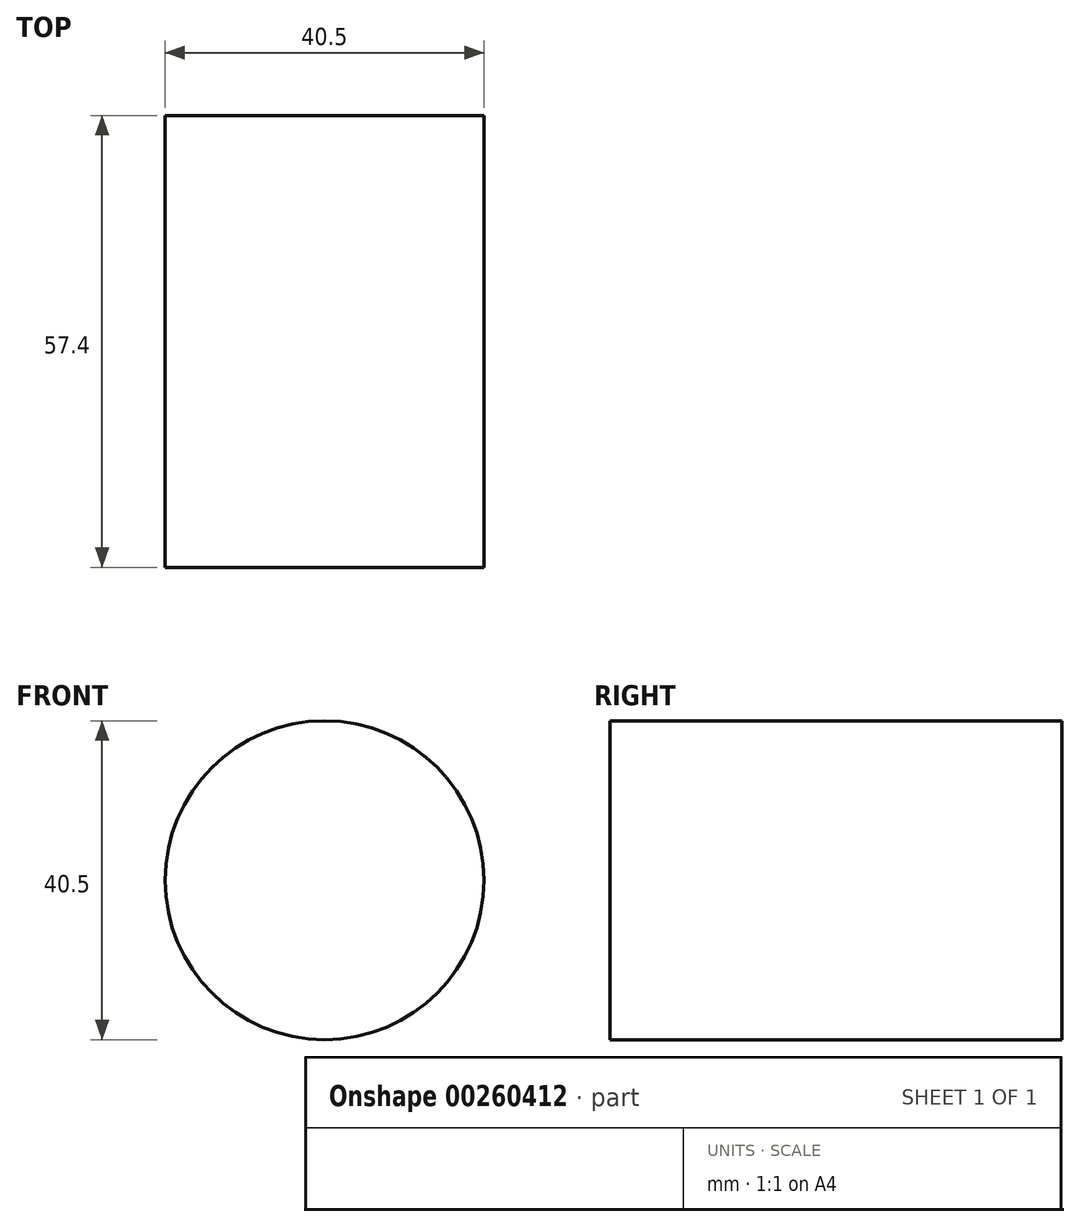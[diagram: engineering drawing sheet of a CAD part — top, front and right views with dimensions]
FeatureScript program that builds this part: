
annotation { "Feature Type Name" : "Feature", "Feature Type Description" : "" }
export const myFeature = defineFeature(function(context is Context, id is Id, definition is map)
    precondition{}
    {
        {
            var Q0;
            Q0=qCreatedBy(makeId("Front.planeOp"),FACE);
            var sketch = newSketch(context, id + "F0", { "sketchPlane" : qUnion([Q0])});
            skCircle(sketch, "E0", {"center": v(0, 0) * mm, "radius": 20.25 * mm});
            skLineSegment(sketch, "E1", {"start": v(0, 0) * mm, "end": v(16.78, 11.33) * mm});
            skSolve(sketch);
        }
        {
            var Q0;
            Q0=makeQuery(id+"F0.imprint","IMPRINT",FACE,{"disambiguationData":[TD([[makeQuery(id+"F0.imprint","IMPRINT",EDGE,{"derivedFrom":sQuery(id+"F0.wireOp",EDGE,"E0")}),1.0]])]});
            extrude(context, id + "F1", {"entities" : qUnion([Q0]), "depth" : 57.4 * mm});
        }
    });
